# Revit family: SoapDispenser-Vitra-EternitySeries-A4487657
name_source: partatom
category: Plumbing Fixtures
revit_build: Autodesk Revit 2017 (Build: 20160225_1515(x64)
units: mm (PartAtom-declared; Revit-internal decimal feet)

## family parameters
Cut with Voids When Loaded = No
Host = Face
OmniClass Number = 23.45.05.14.99
OmniClass Title = Other Sanitary Washing Plumbing Fixtures
Part Type = Normal
Room Calculation Point = No
Round Connector Dimension = Use Diameter
Shared = Yes

## types (8) — shared parameters
BIMobject category = Sanitary - Dispensers
CW Connection = No
Depth(mm) = 100 mm  [stored 0.328084 ft]
Description = Eternity Liquid Soap Dispenser
Design country = Turkey
HW Connection = No
Height(mm) = 160 mm  [stored 0.524934 ft]
IFC Classification = Sanitary Terminal
Manufacturer = Vitra
Manufacturer name = Vitra
Masterformat 2014 Code = 12 00 00
Masterformat 2014 Description = Furnishings
MountingType = Wall-mounted
NBS Referans Code = 35-76-80
NBS Referans Description = Soap Dispensers
Nominal height = 0.000
Nominal width = 0.000
OmniClass Code = 23-31 25 29 13
OmniClass Description = Hand Soap Dispensers
Product Type = Built-in Liquid Soap Dispenser
Product certification = https://vitraglobal.com
Product data url = https://www.vitraglobal.com
Product family = EternitySeries
Product group = Liquid Soap Dispenser
Technical description = https://www.vitra.com.tr
UNSPSC Code = 301815
UNSPSC Description = Sanitary ware
URL = https://vitraglobal.com
Uniclass 1.4 Code = L8246
Uniclass 1.4 Description = Soap holders/dispensers
Uniclass 2.0 Code = PR-35-76-80
Uniclass 2.0 Description = Soap Dispensers
Uniclass 2015 Code = Pr_40_70_22_81
Uniclass 2015 Name = Soap dispensers
Uniformat II Code = E20
Uniformat II Description = FURNISHINGS
Vent Connection = No
Warranty Period (Year) = 5 years
Waste Connection = No
Weight Net (kg) = 1,054
Width(mm) = 70 mm
Youtube = https://www.youtube.com
zero-valued in all types: CWFU, Cost, Default Elevation, HWFU, WFU

## per-type parameters (varying)
| type | Article No. (default) | Coating Material | Color | Model | Product SKU | Second Material |
| LiquidSoapDispenser-Vitra-EternitySeries-A4487657 | A4487657 | Chrome | Chrome | A4487657 | A4487657 | White |
| LiquidSoapDispenser-Vitra-EternitySeries-A4487657EXP | A4487657EXP | Chrome | Chrome | A4487657EXP | A4487657EXP | White |
| LiquidSoapDispenser-Vitra-EternitySeries-A4487658 | A4487658 | Chrome | Black | A4487658 | A4487658 | Black |
| LiquidSoapDispenser-Vitra-EternitySeries-A4487658EXP | A4487658EXP | Chrome | Black | A4487658EXP | A4487658EXP | Black |
| LiquidSoapDispenser-Vitra-EternitySeries-A4487664 | A4487664 | Gold | Black | A4487664 | A4487664 | Black |
| LiquidSoapDispenser-Vitra-EternitySeries-A4487664EXP | A4487664EXP | Gold | Black | A4487664EXP | A4487664EXP | Black |
| LiquidSoapDispenser-Vitra-EternitySeries-A4487627 | A4487627 | Bakır | White | A4487627 | A4487627 | White |
| LiquidSoapDispenser-Vitra-EternitySeries-A4487628 | A4487628 | Bakır | Black | A4487628 | A4487628 | Black |

note: [stored X ft] marks values corroborated as IEEE doubles in the binary element streams (Revit-internal decimal feet)

## geometry (parser evidence)
native form markers: Sweep x3
no freeform markers — native parametric forms only
